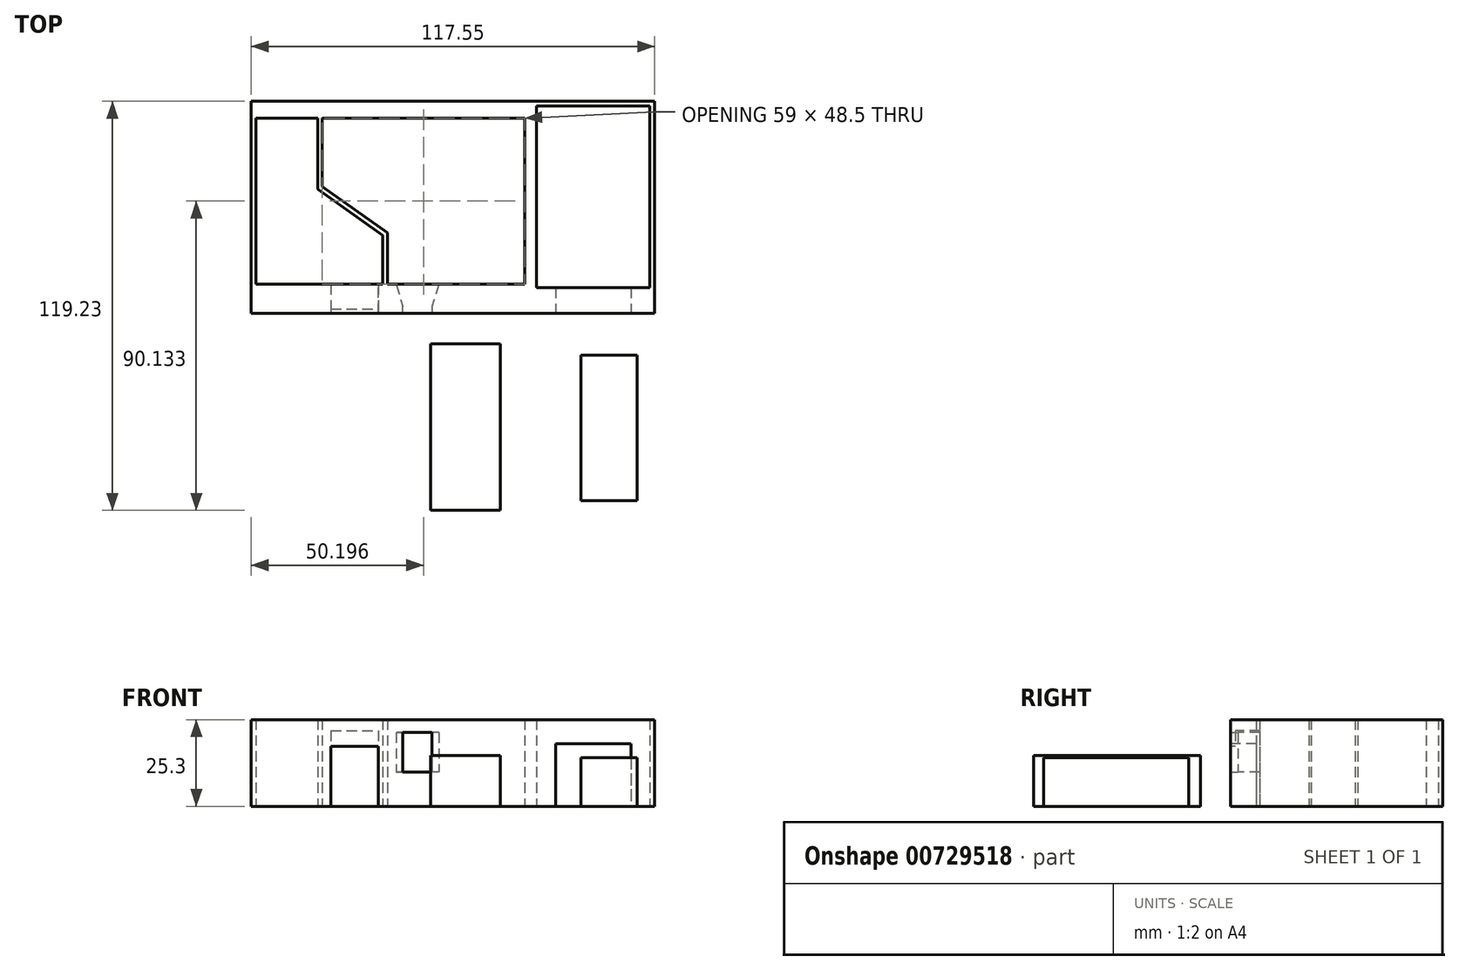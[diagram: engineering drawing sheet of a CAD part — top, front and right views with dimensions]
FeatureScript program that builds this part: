
annotation { "Feature Type Name" : "Feature", "Feature Type Description" : "" }
export const myFeature = defineFeature(function(context is Context, id is Id, definition is map)
    precondition{}
    {
        {
            var Q0;
            Q0=qCreatedBy(makeId("Top.planeOp"),FACE);
            var sketch = newSketch(context, id + "F0", { "sketchPlane" : qUnion([Q0])});
            skLineSegment(sketch, "E0", {"start": v(30.44, 23.02) * mm, "end": v(63.44, 23.02) * mm});
            skLineSegment(sketch, "E1", {"start": v(63.44, 23.02) * mm, "end": v(63.44, -29.98) * mm});
            skLineSegment(sketch, "E2", {"start": v(30.44, 23.02) * mm, "end": v(30.44, -29.98) * mm});
            skLineSegment(sketch, "E3", {"start": v(30.44, -29.98) * mm, "end": v(35.94, -29.98) * mm});
            skLineSegment(sketch, "E4", {"start": v(63.44, -29.98) * mm, "end": v(57.94, -29.98) * mm});
            skLineSegment(sketch, "E5.0", {"start": v(64.79, 24.37) * mm, "end": v(64.79, -37.48) * mm});
            skLineSegment(sketch, "E5.1", {"start": v(-33.41, 24.37) * mm, "end": v(64.79, 24.37) * mm});
            skLineSegment(sketch, "E6.0", {"start": v(64.79, -37.48) * mm, "end": v(57.94, -37.48) * mm});
            skLineSegment(sketch, "E7", {"start": v(57.94, -29.98) * mm, "end": v(57.94, -37.48) * mm});
            skLineSegment(sketch, "E8.0", {"start": v(-0.06, -37.48) * mm, "end": v(35.94, -37.48) * mm});
            skLineSegment(sketch, "E9", {"start": v(35.94, -29.98) * mm, "end": v(35.94, -37.48) * mm});
            skLineSegment(sketch, "E10", {"start": v(-0.06, -37.48) * mm, "end": v(-0.06, -35.37) * mm});
            skLineSegment(sketch, "E11", {"start": v(-0.06, -35.37) * mm, "end": v(1.94, -28.98) * mm});
            skLineSegment(sketch, "E12", {"start": v(1.94, -28.98) * mm, "end": v(26.94, -28.98) * mm});
            skLineSegment(sketch, "E13", {"start": v(26.94, -28.98) * mm, "end": v(26.94, 19.52) * mm});
            skLineSegment(sketch, "E14", {"start": v(26.94, 19.52) * mm, "end": v(-32.06, 19.52) * mm});
            skLineSegment(sketch, "E15", {"start": v(-32.06, 19.52) * mm, "end": v(-32.06, -0.48) * mm});
            skLineSegment(sketch, "E16", {"start": v(-32.06, -0.48) * mm, "end": v(-13.06, -13.98) * mm});
            skLineSegment(sketch, "E17", {"start": v(-13.06, -13.98) * mm, "end": v(-13.06, -28.98) * mm});
            skLineSegment(sketch, "E18", {"start": v(-13.06, -28.98) * mm, "end": v(-10.56, -28.98) * mm});
            skLineSegment(sketch, "E19", {"start": v(-8.56, -35.37) * mm, "end": v(-10.56, -28.98) * mm});
            skLineSegment(sketch, "E20", {"start": v(-8.56, -35.37) * mm, "end": v(-8.56, -37.48) * mm});
            skLineSegment(sketch, "E21.0", {"start": v(-14.41, -14.67) * mm, "end": v(-14.41, -37.48) * mm});
            skLineSegment(sketch, "E21.1", {"start": v(-33.41, -1.17) * mm, "end": v(-14.41, -14.67) * mm});
            skLineSegment(sketch, "E21.2", {"start": v(-33.41, 19.52) * mm, "end": v(-33.41, -1.17) * mm});
            skLineSegment(sketch, "E22", {"start": v(-8.56, -37.48) * mm, "end": v(-14.41, -37.48) * mm});
            skLineSegment(sketch, "E23", {"start": v(-33.41, 19.52) * mm, "end": v(-51.41, 19.52) * mm});
            skLineSegment(sketch, "E24", {"start": v(-51.41, 19.52) * mm, "end": v(-51.41, -28.98) * mm});
            skLineSegment(sketch, "E25", {"start": v(-51.41, -28.98) * mm, "end": v(-29.56, -28.98) * mm});
            skLineSegment(sketch, "E26", {"start": v(-29.56, -28.98) * mm, "end": v(-29.56, -37.48) * mm});
            skLineSegment(sketch, "E27", {"start": v(-29.56, -37.48) * mm, "end": v(-52.76, -37.48) * mm});
            skLineSegment(sketch, "E28", {"start": v(-52.76, -37.48) * mm, "end": v(-52.76, 24.37) * mm});
            skLineSegment(sketch, "E29", {"start": v(-52.76, 24.37) * mm, "end": v(-33.41, 24.37) * mm});
            skLineSegment(sketch, "E30.bottom", {"start": v(-14.41, -37.48) * mm, "end": v(-15.76, -37.48) * mm});
            skLineSegment(sketch, "E30.top", {"start": v(-14.41, -28.98) * mm, "end": v(-15.76, -28.98) * mm});
            skLineSegment(sketch, "E30.left", {"start": v(-14.41, -37.48) * mm, "end": v(-14.41, -28.98) * mm});
            skLineSegment(sketch, "E30.right", {"start": v(-15.76, -37.48) * mm, "end": v(-15.76, -28.98) * mm});
            skSolve(sketch);
        }
        {
            var Q0;
            Q0 = qSketchRegion(id + "F0", true);
            extrude(context, id + "F1", {"entities" : qUnion([Q0]), "depth" : 25.3 * mm, "offsetDistance" : 25 * mm});
        }
        {
            var Q0;
            Q0=makeQuery(id+"F1.opExtrude","SWEPT_FACE",FACE,{"disambiguationData":[OSD([sQuery(id+"F0.wireOp",EDGE,"E8.0")])]});
            var sketch = newSketch(context, id + "F2", { "sketchPlane" : qUnion([Q0])});
            skLineSegment(sketch, "E31.bottom", {"start": v(35.94, 25.3) * mm, "end": v(57.94, 25.3) * mm});
            skLineSegment(sketch, "E31.top", {"start": v(35.94, 18.3) * mm, "end": v(57.94, 18.3) * mm});
            skLineSegment(sketch, "E31.left", {"start": v(35.94, 25.3) * mm, "end": v(35.94, 18.3) * mm});
            skLineSegment(sketch, "E31.right", {"start": v(57.94, 25.3) * mm, "end": v(57.94, 18.3) * mm});
            skSolve(sketch);
        }
        {
            var Q0;
            Q0 = qSketchRegion(id + "F2", true);
            var Q1;
            Q1=makeQuery(id+"F1.opExtrude","CAP_VERTEX",VERTEX,{"disambiguationData":[OSD([sQuery(id+"F0.wireOp",EDGE,"E3"),sQuery(id+"F0.wireOp",EDGE,"E9")])],"isStart":false});
            extrude(context, id + "F3", {"entities" : qUnion([Q0]), "operationType" : NewBodyOperationType.ADD, "endBound" : BoundingType.UP_TO_VERTEX, "oppositeDirection" : true, "depth" : 25 * mm, "endBoundEntityVertex" : qUnion([Q1]), "offsetDistance" : 25 * mm});
        }
        {
            var Q0;
            Q0=makeQuery(id+"F1.opExtrude","SWEPT_FACE",FACE,{"disambiguationData":[OSD([sQuery(id+"F0.wireOp",EDGE,"E12")])]});
            var sketch = newSketch(context, id + "F4", { "sketchPlane" : qUnion([Q0])});
            skLineSegment(sketch, "E32.bottom", {"start": v(-1.94, 25.3) * mm, "end": v(10.56, 25.3) * mm});
            skLineSegment(sketch, "E32.top", {"start": v(-1.94, 21.5) * mm, "end": v(10.56, 21.5) * mm});
            skLineSegment(sketch, "E32.left", {"start": v(-1.94, 25.3) * mm, "end": v(-1.94, 21.5) * mm});
            skLineSegment(sketch, "E32.right", {"start": v(10.56, 25.3) * mm, "end": v(10.56, 21.5) * mm});
            skLineSegment(sketch, "E33.bottom", {"start": v(-1.94, 0) * mm, "end": v(10.56, 0) * mm});
            skLineSegment(sketch, "E33.top", {"start": v(-1.94, 10) * mm, "end": v(10.56, 10) * mm});
            skLineSegment(sketch, "E33.left", {"start": v(-1.94, 0) * mm, "end": v(-1.94, 10) * mm});
            skLineSegment(sketch, "E33.right", {"start": v(10.56, 0) * mm, "end": v(10.56, 10) * mm});
            skSolve(sketch);
        }
        {
            var Q0;
            Q0 = qSketchRegion(id + "F4", true);
            var Q1;
            Q1=makeQuery(id+"F1.opExtrude","CAP_VERTEX",VERTEX,{"disambiguationData":[OSD([sQuery(id+"F0.wireOp",EDGE,"E8.0"),sQuery(id+"F0.wireOp",EDGE,"E10")])],"isStart":false});
            extrude(context, id + "F5", {"entities" : qUnion([Q0]), "operationType" : NewBodyOperationType.ADD, "endBound" : BoundingType.UP_TO_VERTEX, "oppositeDirection" : true, "depth" : 25 * mm, "endBoundEntityVertex" : qUnion([Q1]), "offsetDistance" : 25 * mm});
        }
        {
            var Q0;
            Q0=makeQuery(id+"F1.opExtrude","SWEPT_FACE",FACE,{"disambiguationData":[OSD([sQuery(id+"F0.wireOp",EDGE,"E27")])]});
            var sketch = newSketch(context, id + "F6", { "sketchPlane" : qUnion([Q0])});
            skLineSegment(sketch, "E34.bottom", {"start": v(-29.56, 25.3) * mm, "end": v(-15.76, 25.3) * mm});
            skLineSegment(sketch, "E34.top", {"start": v(-29.56, 22) * mm, "end": v(-15.76, 22) * mm});
            skLineSegment(sketch, "E34.left", {"start": v(-29.56, 25.3) * mm, "end": v(-29.56, 22) * mm});
            skLineSegment(sketch, "E34.right", {"start": v(-15.76, 25.3) * mm, "end": v(-15.76, 22) * mm});
            skLineSegment(sketch, "E35.top", {"start": v(-29.56, 17.5) * mm, "end": v(-15.76, 17.5) * mm});
            skLineSegment(sketch, "E35.left", {"start": v(-29.56, 22) * mm, "end": v(-29.56, 17.5) * mm});
            skLineSegment(sketch, "E35.right", {"start": v(-15.76, 22) * mm, "end": v(-15.76, 17.5) * mm});
            skSolve(sketch);
        }
        {
            var Q0;
            Q0=makeQuery(id+"F6.imprint","IMPRINT",FACE,{"disambiguationData":[TD([[makeQuery(id+"F6.imprint","IMPRINT",EDGE,{"derivedFrom":sQuery(id+"F6.wireOp",EDGE,"E34.bottom")}),-1.0]])]});
            var Q1;
            Q1=makeQuery(id+"F1.opExtrude","CAP_VERTEX",VERTEX,{"disambiguationData":[OSD([sQuery(id+"F0.wireOp",EDGE,"E25"),sQuery(id+"F0.wireOp",EDGE,"E26")])],"isStart":false});
            extrude(context, id + "F7", {"entities" : qUnion([Q0]), "operationType" : NewBodyOperationType.ADD, "endBound" : BoundingType.UP_TO_VERTEX, "oppositeDirection" : true, "depth" : 25 * mm, "endBoundEntityVertex" : qUnion([Q1]), "offsetDistance" : 25 * mm});
        }
        {
            var Q0;
            Q0=makeQuery(id+"F6.imprint","IMPRINT",FACE,{"disambiguationData":[TD([[makeQuery(id+"F6.imprint","IMPRINT",EDGE,{"derivedFrom":sQuery(id+"F6.wireOp",EDGE,"E34.top")}),-1.0]])]});
            extrude(context, id + "F8", {"entities" : qUnion([Q0]), "operationType" : NewBodyOperationType.ADD, "oppositeDirection" : true, "depth" : 1.35 * mm, "offsetDistance" : 25 * mm});
        }
        {
            var Q0;
            Q0=qCreatedBy(makeId("Top.planeOp"),FACE);
            var sketch = newSketch(context, id + "F9", { "sketchPlane" : qUnion([Q0])});
            skLineSegment(sketch, "E36.bottom", {"start": v(-0.42, -46.3) * mm, "end": v(19.89, -46.3) * mm});
            skLineSegment(sketch, "E36.top", {"start": v(-0.42, -94.86) * mm, "end": v(19.89, -94.86) * mm});
            skLineSegment(sketch, "E36.left", {"start": v(-0.42, -46.3) * mm, "end": v(-0.42, -94.86) * mm});
            skLineSegment(sketch, "E36.right", {"start": v(19.89, -46.3) * mm, "end": v(19.89, -94.86) * mm});
            skSolve(sketch);
        }
        {
            var Q0;
            Q0 = qSketchRegion(id + "F9", true);
            extrude(context, id + "F10", {"entities" : qUnion([Q0]), "depth" : 14.77 * mm, "offsetDistance" : 25 * mm});
        }
        {
            var Q0;
            Q0=qCreatedBy(makeId("Top.planeOp"),FACE);
            var sketch = newSketch(context, id + "F11", { "sketchPlane" : qUnion([Q0])});
            skLineSegment(sketch, "E37.bottom", {"start": v(43.35, -92.03) * mm, "end": v(59.7, -92.03) * mm});
            skLineSegment(sketch, "E37.top", {"start": v(43.35, -49.66) * mm, "end": v(59.7, -49.66) * mm});
            skLineSegment(sketch, "E37.left", {"start": v(43.35, -92.03) * mm, "end": v(43.35, -49.66) * mm});
            skLineSegment(sketch, "E37.right", {"start": v(59.7, -92.03) * mm, "end": v(59.7, -49.66) * mm});
            skSolve(sketch);
        }
        {
            var Q0;
            Q0 = qSketchRegion(id + "F11", true);
            extrude(context, id + "F12", {"entities" : qUnion([Q0]), "depth" : 14.2 * mm, "offsetDistance" : 25 * mm});
        }
    });
